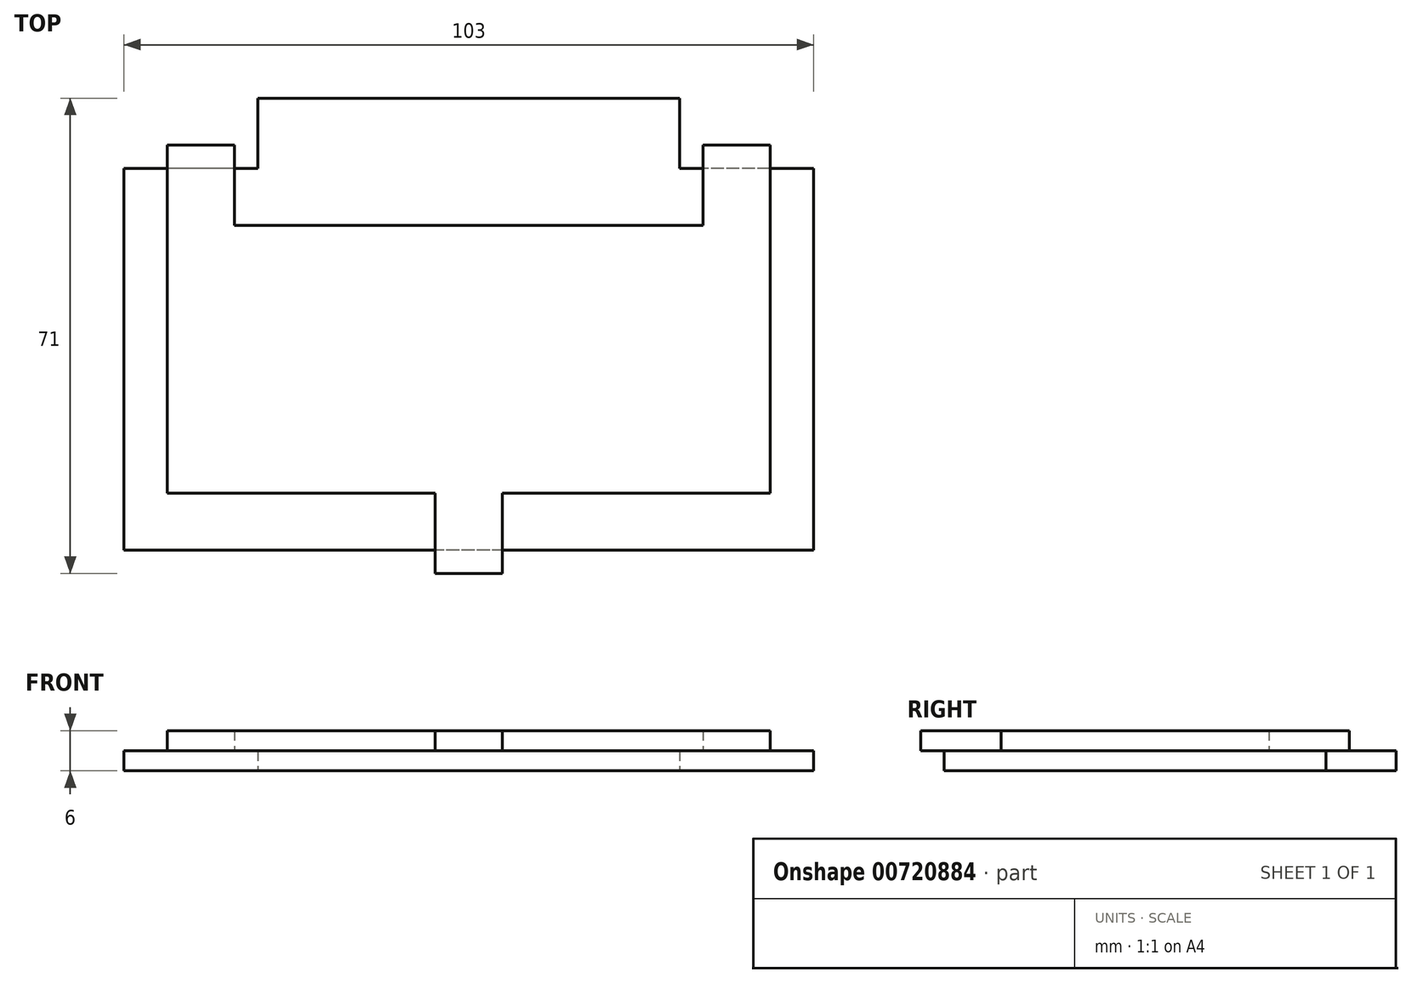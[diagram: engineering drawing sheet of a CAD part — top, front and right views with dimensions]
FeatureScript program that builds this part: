
annotation { "Feature Type Name" : "Feature", "Feature Type Description" : "" }
export const myFeature = defineFeature(function(context is Context, id is Id, definition is map)
    precondition{}
    {
        {
            var Q0;
            Q0=qCreatedBy(makeId("Top.planeOp"),FACE);
            var sketch = newSketch(context, id + "F0", { "sketchPlane" : qUnion([Q0])});
            skLineSegment(sketch, "E0.bottom", {"start": v(51.5, 28.5) * mm, "end": v(-51.5, 28.5) * mm});
            skLineSegment(sketch, "E0.top", {"start": v(51.5, -28.5) * mm, "end": v(-51.5, -28.5) * mm});
            skLineSegment(sketch, "E0.left", {"start": v(51.5, 28.5) * mm, "end": v(51.5, -28.5) * mm});
            skLineSegment(sketch, "E0.right", {"start": v(-51.5, 28.5) * mm, "end": v(-51.5, -28.5) * mm});
            skPoint(sketch, "E0.middle", {"position": v(0, 0) * mm});
            skLineSegment(sketch, "E1.bottom", {"start": v(-31.5, 39) * mm, "end": v(31.5, 39) * mm});
            skLineSegment(sketch, "E1.top", {"start": v(-31.5, 18) * mm, "end": v(31.5, 18) * mm});
            skLineSegment(sketch, "E1.left", {"start": v(-31.5, 39) * mm, "end": v(-31.5, 18) * mm});
            skLineSegment(sketch, "E1.right", {"start": v(31.5, 39) * mm, "end": v(31.5, 18) * mm});
            skPoint(sketch, "E1.middle", {"position": v(0, 28.5) * mm});
            skSolve(sketch);
        }
        {
            var Q0;
            Q0 = qSketchRegion(id + "F0", true);
            extrude(context, id + "F1", {"entities" : qUnion([Q0]), "depth" : 3 * mm, "offsetDistance" : 25 * mm});
        }
        {
            var Q0;
            Q0=makeQuery(id+"F1.opExtrude","CAP_FACE",FACE,{"disambiguationData":[OSD([sQuery(id+"F0.wireOp",EDGE,"E0.bottom"),sQuery(id+"F0.wireOp",EDGE,"E0.top"),sQuery(id+"F0.wireOp",EDGE,"E0.left"),sQuery(id+"F0.wireOp",EDGE,"E0.right"),sQuery(id+"F0.wireOp",EDGE,"E1.bottom"),sQuery(id+"F0.wireOp",EDGE,"E1.left"),sQuery(id+"F0.wireOp",EDGE,"E1.right")])],"isStart":false});
            var sketch = newSketch(context, id + "F2", { "sketchPlane" : qUnion([Q0])});
            skLineSegment(sketch, "E2.bottom", {"start": v(35, 20) * mm, "end": v(-35, 20) * mm});
            skLineSegment(sketch, "E2.top", {"start": v(45, -20) * mm, "end": v(5, -20) * mm});
            skLineSegment(sketch, "E2.left", {"start": v(45, 20) * mm, "end": v(45, -20) * mm});
            skLineSegment(sketch, "E2.right", {"start": v(-45, 20) * mm, "end": v(-45, -20) * mm});
            skPoint(sketch, "E2.middle", {"position": v(0, 0) * mm});
            skLineSegment(sketch, "E3.top", {"start": v(-45, 32) * mm, "end": v(-35, 32) * mm});
            skLineSegment(sketch, "E3.left", {"start": v(-45, 20) * mm, "end": v(-45, 32) * mm});
            skLineSegment(sketch, "E3.right", {"start": v(-35, 20) * mm, "end": v(-35, 32) * mm});
            skLineSegment(sketch, "E4.MirrorCS", {"start": v(35, 20) * mm, "end": v(35, 32) * mm});
            skLineSegment(sketch, "E5.MirrorCS", {"start": v(45, 20) * mm, "end": v(45, 32) * mm});
            skLineSegment(sketch, "E6.MirrorCS", {"start": v(45, 32) * mm, "end": v(35, 32) * mm});
            skLineSegment(sketch, "E7.top", {"start": v(0, -32) * mm, "end": v(-5, -32) * mm});
            skLineSegment(sketch, "E7.right", {"start": v(-5, -20) * mm, "end": v(-5, -32) * mm});
            skLineSegment(sketch, "E8.MirrorCS", {"start": v(5, -20) * mm, "end": v(5, -32) * mm});
            skLineSegment(sketch, "E9.MirrorCS", {"start": v(-45, -20) * mm, "end": v(-5, -20) * mm});
            skLineSegment(sketch, "E10.MirrorCS", {"start": v(0, -32) * mm, "end": v(5, -32) * mm});
            skLineSegment(sketch, "E11.trimOffspring", {"start": v(-5, -20) * mm, "end": v(-45, -20) * mm});
            skLineSegment(sketch, "E12.trimOffspring", {"start": v(5, -20) * mm, "end": v(45, -20) * mm});
            skPoint(sketch, "E7.left.start.orphan", {"position": v(0, -20) * mm});
            skPoint(sketch, "E13.MirrorCS.start.orphan", {"position": v(45, 20) * mm});
            skSolve(sketch);
        }
        {
            var Q0;
            Q0 = qSketchRegion(id + "F2", true);
            extrude(context, id + "F3", {"entities" : qUnion([Q0]), "depth" : 3 * mm, "offsetDistance" : 25 * mm});
        }
    });
